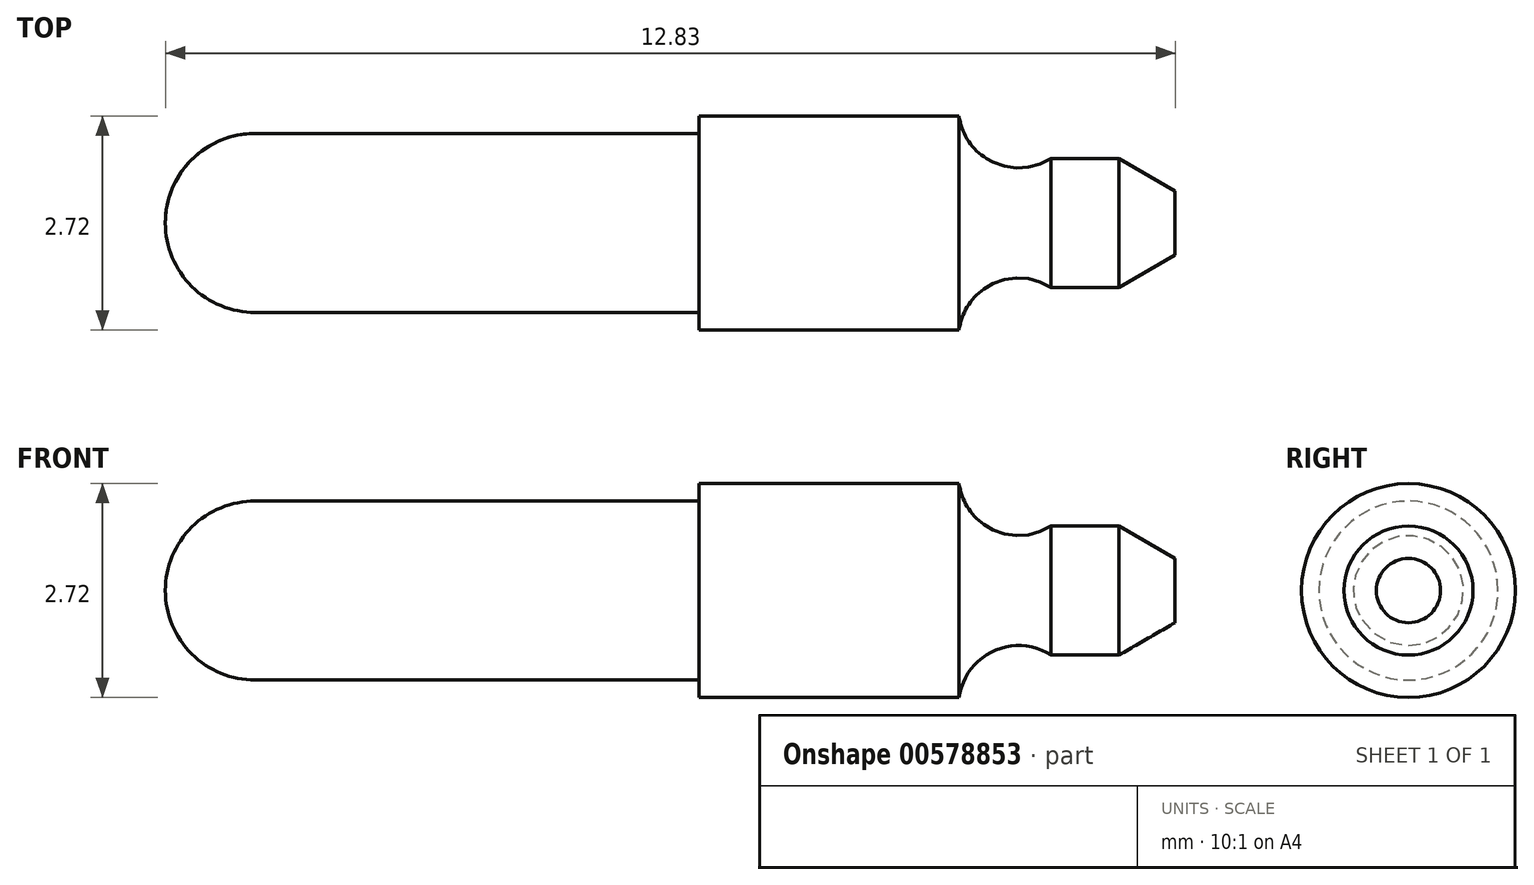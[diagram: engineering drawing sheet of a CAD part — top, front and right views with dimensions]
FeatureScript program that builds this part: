
annotation { "Feature Type Name" : "Feature", "Feature Type Description" : "" }
export const myFeature = defineFeature(function(context is Context, id is Id, definition is map)
    precondition{}
    {
        {
            var Q0;
            Q0=qCreatedBy(makeId("Right.planeOp"),FACE);
            var sketch = newSketch(context, id + "F0", { "sketchPlane" : qUnion([Q0])});
            skCircle(sketch, "E0", {"center": v(0, 0) * mm, "radius": 1.36 * mm});
            skSolve(sketch);
        }
        {
            var Q0;
            Q0=qSketchRegion(id+"F0",true);
            extrude(context, id + "F1", {"entities" : qUnion([Q0]), "depth" : 3.3 * mm});
        }
        {
            var Q0;
            Q0=makeQuery(id+"F1.opExtrude","CAP_FACE",FACE,{"disambiguationData":[OSD([sQuery(id+"F0.wireOp",EDGE,"E0")])],"isStart":true});
            var sketch = newSketch(context, id + "F2", { "sketchPlane" : qUnion([Q0])});
            skCircle(sketch, "E1", {"center": v(0, 0) * mm, "radius": 1.14 * mm});
            skSolve(sketch);
        }
        {
            var Q0;
            Q0=qSketchRegion(id+"F2",true);
            extrude(context, id + "F3", {"entities" : qUnion([Q0]), "operationType" : NewBodyOperationType.ADD, "depth" : 5.64 * mm});
        }
        {
            var Q0;
            Q0=qCreatedBy(makeId("Top.planeOp"),FACE);
            var sketch = newSketch(context, id + "F4", { "sketchPlane" : qUnion([Q0])});
            skLineSegment(sketch, "E2.0", {"start": v(-5.64, 0) * mm, "end": v(-5.64, 1.14) * mm});
            skPoint(sketch, "E3", {"position": v(-5.64, 0) * mm});
            skLineSegment(sketch, "E4", {"start": v(-5.64, 0) * mm, "end": v(-6.78, 0) * mm});
            skArc(sketch, "E5", {"start": v(-5.64, 1.14) * mm, "mid": v(-6.45, 0.8) * mm, "end": v(-6.78, 0) * mm});
            skPoint(sketch, "E6.orphan", {"position": v(-5.64, -1.14) * mm});
            skSolve(sketch);
        }
        {
            var Q0;
            Q0=makeQuery(id+"F4.imprint","IMPRINT",FACE,{"disambiguationData":[TD([[makeQuery(id+"F4.imprint","IMPRINT",EDGE,{"derivedFrom":sQuery(id+"F4.wireOp",EDGE,"E2.0")}),1.0]])]});
            var Q1;
            Q1=sQuery(id+"F4.wireOp",EDGE,"E4");
            revolve(context, id + "F5", {"operationType" : NewBodyOperationType.ADD, "entities" : qUnion([Q0]), "axis" : qUnion([Q1]), "revolveType" : RevolveType.FULL});
        }
        {
            var Q0;
            Q0=qCreatedBy(makeId("Top.planeOp"),FACE);
            var sketch = newSketch(context, id + "F6", { "sketchPlane" : qUnion([Q0])});
            skLineSegment(sketch, "E7.0", {"start": v(3.3, 0) * mm, "end": v(3.3, -1.36) * mm});
            skPoint(sketch, "E8", {"position": v(3.3, 0) * mm});
            skLineSegment(sketch, "E9", {"start": v(4.47, -0.82) * mm, "end": v(5.33, -0.82) * mm});
            skLineSegment(sketch, "E10", {"start": v(5.33, -0.82) * mm, "end": v(6.05, -0.4) * mm});
            skLineSegment(sketch, "E11", {"start": v(6.05, -0.4) * mm, "end": v(6.05, 0) * mm});
            skLineSegment(sketch, "E12", {"start": v(6.05, 0) * mm, "end": v(3.3, 0) * mm});
            skArc(sketch, "E13", {"start": v(4.47, -0.82) * mm, "mid": v(3.74, -0.77) * mm, "end": v(3.3, -1.36) * mm});
            skPoint(sketch, "E14.orphan", {"position": v(3.3, 1.36) * mm});
            skSolve(sketch);
        }
        {
            var Q0;
            Q0=makeQuery(id+"F6.imprint","IMPRINT",FACE,{"disambiguationData":[TD([[makeQuery(id+"F6.imprint","IMPRINT",EDGE,{"derivedFrom":sQuery(id+"F6.wireOp",EDGE,"E9")}),1.0]])]});
            var Q1;
            Q1=sQuery(id+"F6.wireOp",EDGE,"E12");
            revolve(context, id + "F7", {"operationType" : NewBodyOperationType.ADD, "entities" : qUnion([Q0]), "axis" : qUnion([Q1]), "revolveType" : RevolveType.FULL});
        }
    });
